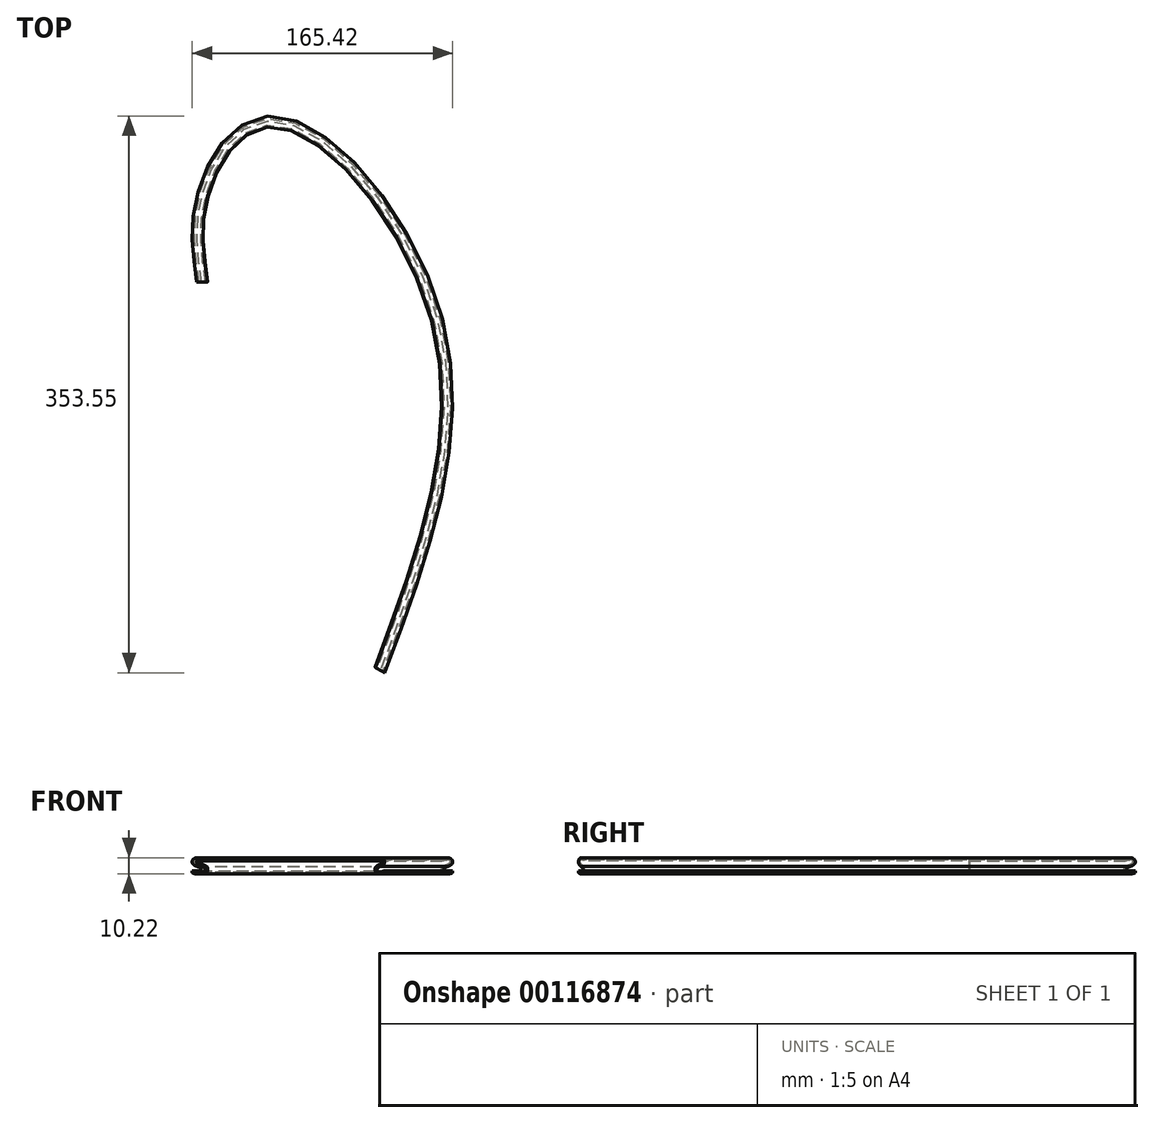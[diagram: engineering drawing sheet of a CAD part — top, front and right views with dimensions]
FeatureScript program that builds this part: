
annotation { "Feature Type Name" : "Feature", "Feature Type Description" : "" }
export const myFeature = defineFeature(function(context is Context, id is Id, definition is map)
    precondition{}
    {
        {
            var Q0;
            Q0=qCreatedBy(makeId("Top.planeOp"),FACE);
            var sketch = newSketch(context, id + "F0", { "sketchPlane" : qUnion([Q0])});
            skFitSpline(sketch, "E0", {"points": [v(0, 0) * mm, v(0, 54.12) * mm, v(40.97, 99.48) * mm, v(143.54, -22.4) * mm, v(108.11, -245.24) * mm], "startDerivative": vector(-45.53, 299.83) * mm, "endDerivative": vector(-239.02, -638.84) * mm});
            skSolve(sketch);
        }
        {
            var Q0;
            Q0=qCreatedBy(makeId("Front.planeOp"),FACE);
            var sketch = newSketch(context, id + "F1", { "sketchPlane" : qUnion([Q0])});
            skText(sketch, "E1", { "text": "s", "fontName": "OpenSans-Regular.ttf"});
            const initialGuessF1  = {"E1": [-0.00693, -0.00785, 1, 0, 0.01326]};
            skSetInitialGuess(sketch, initialGuessF1);
            skSolve(sketch);
        }
        {
            var Q0;
            Q0 = qSketchRegion(id + "F1", true);
            var Q1;
            Q1 = qBodyType(qCreatedBy(id + "F0" ,EDGE), BodyType.WIRE);
            sweep(context, id + "F2", {"profiles" : qUnion([Q0]), "path" : qUnion([Q1])});
        }
    });
